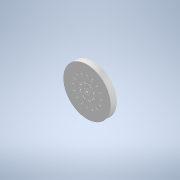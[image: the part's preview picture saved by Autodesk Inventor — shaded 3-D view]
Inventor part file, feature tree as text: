
AUTODESK INVENTOR PART (.ipt)
format: ipt  version: 2020 (Build 240168000, 168)  size: 280,576 bytes
history: native  units: in
note: dims shown in document units (in); Inventor stores cm internally (conversion verified against a paired STEP export)
features: sketch x6, extrude x4, revolve x1
ambient origin geometry x8: Origin, YZ Plane, XZ Plane, XY Plane, X Axis, Y Axis, Z Axis, Center Point
bodies: Solid1 (feature_tree)
feature tree (11):
  extrude  "Extrusion1"  Depth=2.0in TaperAngle=0.0deg
  revolve  "Revolution1"  [1 undecoded]
  sketch  "Sketch3"  dims[d5=11.25in d6=90.0deg]
  extrude  "Extrusion2"  TaperAngle=90.0deg  [1 undecoded]
  extrude  "Extrusion3"  Depth=0.5in
  extrude  "Extrusion4"  Depth=4.7244in TaperAngle=360.0deg
  sketch  "Sketch1"  dims[d0=16.0in d1=2.0in d2=0.0in]
  sketch  "Sketch2"  dims[d3=1.0in d4=7.0in]
  sketch  "Sketch4"  dims[d7=0.5in d8=0.9375in]
  sketch  "Sketch6"  dims[d9=0.2031in d10=4.7244in d12=360.0deg]
  sketch  "Sketch7"  dims[d14=0.0in d15=0.0in d16=0.2031in d17=4.25in d18=0.35in d19=4.735in d20=6.2992in d22=360.0deg d24=0.0in d25=0.0in d26=0.16in d27=2.497in d28=3.1496in d30=360.0deg d32=0.16in d33=2.2545in d34=0.0773in d35=0.35in d36=22.5deg d37=3.1496in d39=360.0deg d41=3.1496in d43=360.0deg d45=0.2319in d46=3.1496in d48=360.0deg d50=0.0in d51=0.0in]
note: 2 required parameter values undecoded (feature->parameter linkage not recoverable at this tier; creation-order binding heuristic only, values carry confidence <= 0.55)